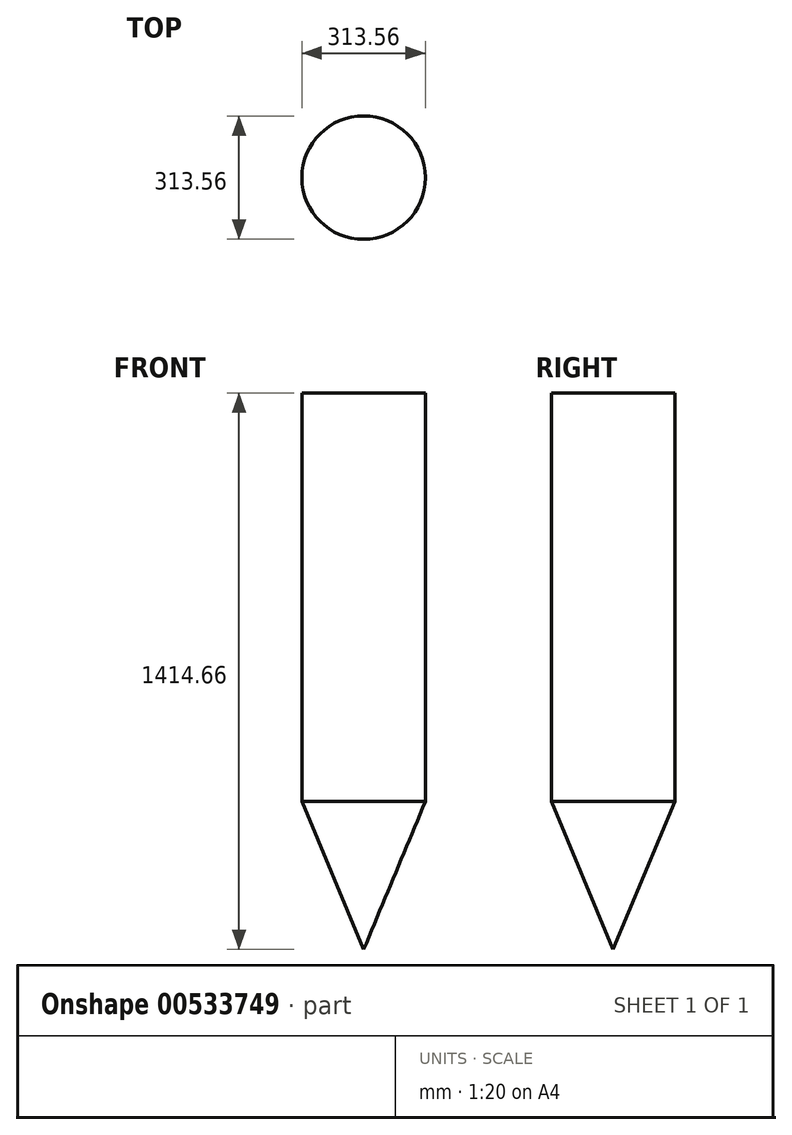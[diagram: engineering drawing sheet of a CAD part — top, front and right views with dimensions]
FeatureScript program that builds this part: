
annotation { "Feature Type Name" : "Feature", "Feature Type Description" : "" }
export const myFeature = defineFeature(function(context is Context, id is Id, definition is map)
    precondition{}
    {
        {
            var Q0;
            Q0=qCreatedBy(makeId("Top.planeOp"),FACE);
            var sketch = newSketch(context, id + "F0", { "sketchPlane" : qUnion([Q0])});
            skCircle(sketch, "E0", {"center": v(0, 0) * mm, "radius": 156.78 * mm});
            skSolve(sketch);
        }
        {
            var Q0;
            Q0=qCreatedBy(makeId("Front.planeOp"),FACE);
            var sketch = newSketch(context, id + "F1", { "sketchPlane" : qUnion([Q0])});
            skPoint(sketch, "E1", {"position": v(0, 713.93) * mm});
            skPoint(sketch, "E2", {"position": v(0, 1003.77) * mm});
            skSolve(sketch);
        }
        {
            var Q0;
            Q0=makeQuery(id+"F0.imprint","IMPRINT",FACE,{"disambiguationData":[TD([[makeQuery(id+"F0.imprint","IMPRINT",EDGE,{"derivedFrom":sQuery(id+"F0.wireOp",EDGE,"E0")}),1.0]])]});
            extrude(context, id + "F2", {"entities" : qUnion([Q0]), "depth" : 723.1 * mm, "offsetDistance" : 25.4 * mm});
        }
        {
            var Q0;
            Q0=qCreatedBy(makeId("Right.planeOp"),FACE);
            var sketch = newSketch(context, id + "F3", { "sketchPlane" : qUnion([Q0])});
            skPoint(sketch, "E3", {"position": v(0, -691.56) * mm});
            skSolve(sketch);
        }
        {
            var Q0;
            Q0=makeQuery(id+"F2.opExtrude","CAP_FACE",FACE,{"disambiguationData":[OSD([sQuery(id+"F0.wireOp",EDGE,"E0")])],"isStart":true});
            extrude(context, id + "F4", {"entities" : qUnion([Q0]), "operationType" : NewBodyOperationType.ADD, "depth" : 289.73 * mm, "offsetDistance" : 25.4 * mm});
        }
        {
            var Q0;
            Q0=makeQuery(id+"F4.opExtrude","CAP_FACE",FACE,{"disambiguationData":[OSD([sQuery(id+"F0.wireOp",EDGE,"E0")])],"isStart":false});
            extrude(context, id + "F5", {"entities" : qUnion([Q0]), "operationType" : NewBodyOperationType.ADD, "depth" : 25.4 * mm, "offsetDistance" : 25.4 * mm});
        }
        {
            var Q1;
            Q1=makeQuery(id+"F5.opExtrude","CAP_FACE",FACE,{"disambiguationData":[OSD([sQuery(id+"F0.wireOp",EDGE,"E0")])],"isStart":false});
            var Q2;
            Q2=sQuery(id+"F3.wireOp",VERTEX,"E3");
            loft(context, id + "F6", {"operationType" : NewBodyOperationType.ADD, "sheetProfilesArray" : [{ "sheetProfileEntities" : qUnion([Q1]) }, { "sheetProfileEntities" : qUnion([Q2]) }]});
        }
    });
